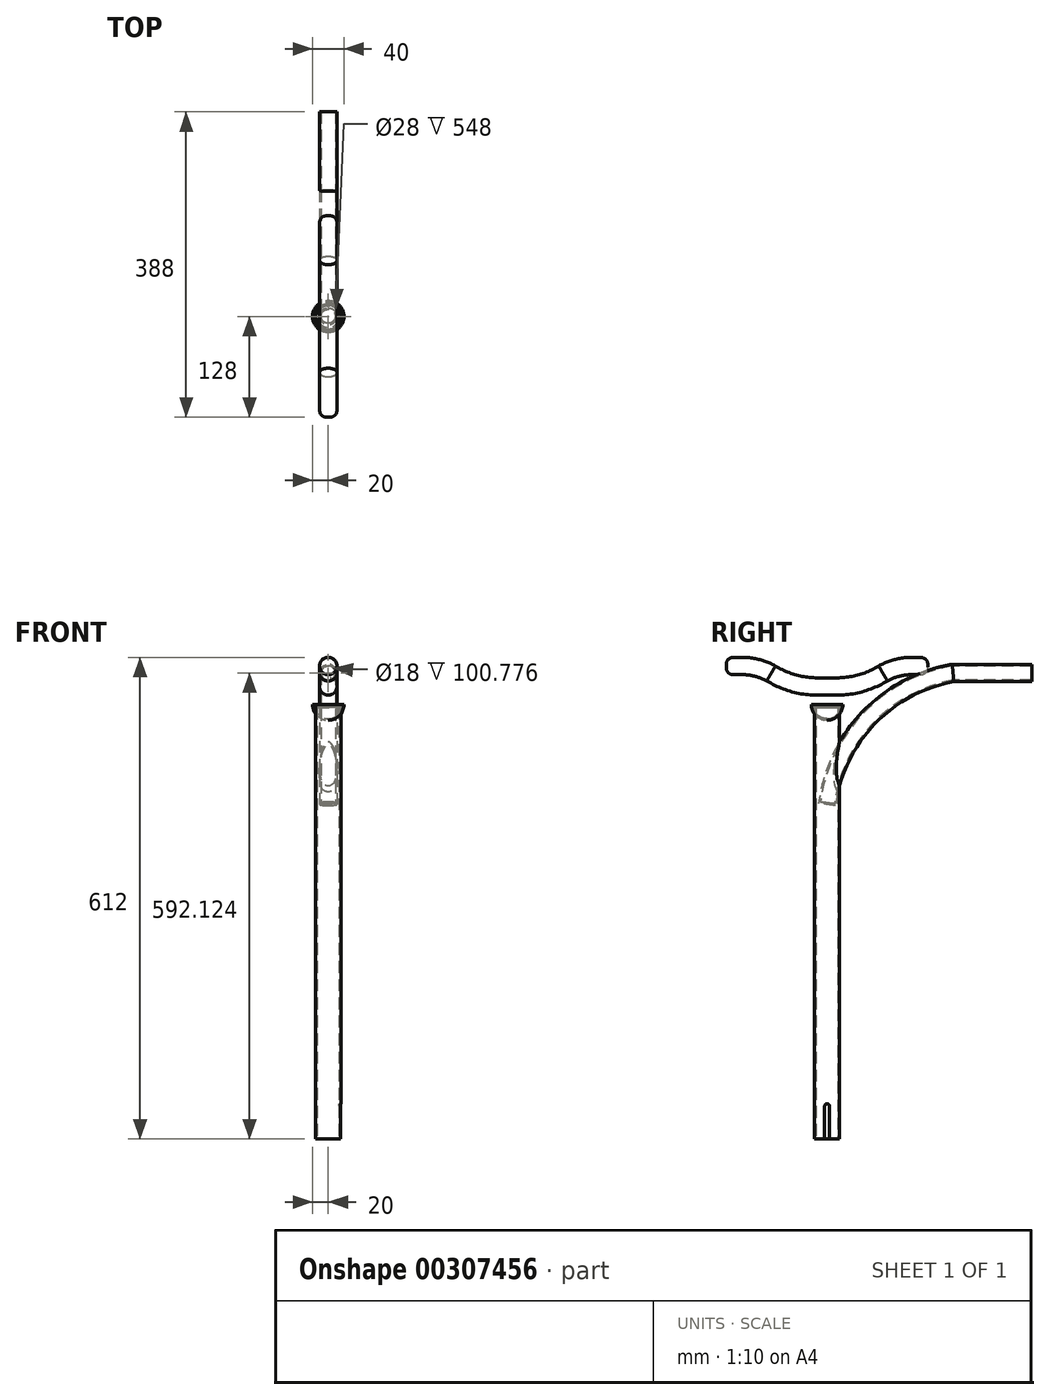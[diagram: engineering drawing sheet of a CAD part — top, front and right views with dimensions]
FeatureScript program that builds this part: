
annotation { "Feature Type Name" : "Feature", "Feature Type Description" : "" }
export const myFeature = defineFeature(function(context is Context, id is Id, definition is map)
    precondition{}
    {
        {
            var Q0;
            Q0=qCreatedBy(makeId("Top.planeOp"),FACE);
            var sketch = newSketch(context, id + "F0", { "sketchPlane" : qUnion([Q0])});
            skCircle(sketch, "E0", {"center": v(0, 0) * mm, "radius": 16 * mm});
            skSolve(sketch);
        }
        {
            var Q0;
            Q0 = qSketchRegion(id + "F0", true);
            extrude(context, id + "F1", {"entities" : qUnion([Q0]), "depth" : 550 * mm, "offsetDistance" : 25 * mm});
        }
        {
            var Q0;
            Q0=makeQuery(id+"F1.opExtrude","CAP_FACE",FACE,{"disambiguationData":[OSD([sQuery(id+"F0.wireOp",EDGE,"E0")])],"isStart":true});
            shell(context, id + "F2", {"entities" : qUnion([Q0]), "thickness" : 2 * mm});
        }
        {
            var Q0;
            Q0=qCreatedBy(makeId("Right.planeOp"),FACE);
            var sketch = newSketch(context, id + "F3", { "sketchPlane" : qUnion([Q0])});
            skLineSegment(sketch, "E1.bottom", {"start": v(0, 45) * mm, "end": v(0, 45) * mm});
            skLineSegment(sketch, "E1.top", {"start": v(-3, 0) * mm, "end": v(3, 0) * mm});
            skLineSegment(sketch, "E1.left", {"start": v(-3, 42) * mm, "end": v(-3, 0) * mm});
            skLineSegment(sketch, "E1.right", {"start": v(3, 42) * mm, "end": v(3, 0) * mm});
            skPoint(sketch, "E2.visualSharp", {"position": v(3, 45) * mm});
            skArc(sketch, "E2.filletArc", {"start": v(3, 42) * mm, "mid": v(2.12, 44.12) * mm, "end": v(0, 45) * mm});
            skPoint(sketch, "E3.visualSharp", {"position": v(-3, 45) * mm});
            skArc(sketch, "E3.filletArc", {"start": v(0, 45) * mm, "mid": v(-2.12, 44.12) * mm, "end": v(-3, 42) * mm});
            skSolve(sketch);
        }
        {
            var Q0;
            Q0 = qSketchRegion(id + "F3", true);
            extrude(context, id + "F4", {"entities" : qUnion([Q0]), "operationType" : NewBodyOperationType.REMOVE, "endBound" : BoundingType.THROUGH_ALL, "depth" : 25 * mm, "offsetDistance" : 25 * mm});
        }
        {
            var Q0;
            Q0=qCreatedBy(makeId("Right.planeOp"),FACE);
            var sketch = newSketch(context, id + "F5", { "sketchPlane" : qUnion([Q0])});
            skArc(sketch, "E4", {"start": v(160, 592.12) * mm, "mid": v(52.58, 534.92) * mm, "end": v(0, 425.16) * mm});
            skLineSegment(sketch, "E5", {"start": v(160, 592.12) * mm, "end": v(260, 592.12) * mm});
            skSolve(sketch);
        }
        {
            var Q0;
            Q0=qCreatedBy(makeId("Front.planeOp"),FACE);
            var Q1;
            Q1=sQuery(id+"F5.wireOp",VERTEX,"E5.end");
            cPlane(context, id + "F6", {"entities" : qUnion([Q0, Q1]), "cplaneType" : CPlaneType.PLANE_POINT, "offset" : 25 * mm, "width" : 150 * mm, "height" : 150 * mm});
        }
        {
            var Q0;
            Q0=qCreatedBy(id+"F6.planeOp",FACE);
            var sketch = newSketch(context, id + "F7", { "sketchPlane" : qUnion([Q0])});
            skCircle(sketch, "E6", {"center": v(0, 592.12) * mm, "radius": 11 * mm});
            skSolve(sketch);
        }
        {
            var Q0;
            Q0 = qSketchRegion(id + "F7", true);
            var Q1;
            Q1 = qConstructionFilter(qBodyType(qCreatedBy(id + "F5" ,EDGE), BodyType.WIRE), ConstructionObject.NO);
            sweep(context, id + "F8", {"operationType" : NewBodyOperationType.ADD, "profiles" : qUnion([Q0]), "path" : qUnion([Q1])});
        }
        {
            var Q0;
            Q0=makeQuery(id+"F8.opSweep","CAP_FACE",FACE,{"disambiguationData":[OSD([sQuery(id+"F5.wireOp",VERTEX,"E5.end"),sQuery(id+"F7.wireOp",EDGE,"E6")])],"isStart":true});
            shell(context, id + "F9", {"entities" : qUnion([Q0]), "thickness" : 2 * mm});
        }
        {
            var Q0;
            Q0=qCreatedBy(makeId("Right.planeOp"),FACE);
            var sketch = newSketch(context, id + "F10", { "sketchPlane" : qUnion([Q0])});
            skLineSegment(sketch, "E7", {"start": v(-128, 601) * mm, "end": v(-108, 601) * mm});
            skArc(sketch, "E8", {"start": v(-71.14, 591.58) * mm, "mid": v(-88.98, 598.6) * mm, "end": v(-108, 601) * mm});
            skLineSegment(sketch, "E9", {"start": v(-12.5, 575) * mm, "end": v(0, 575) * mm});
            skLineSegment(sketch, "E10", {"start": v(0, 0) * mm, "end": v(0, 575) * mm, "construction": true});
            skArc(sketch, "E11", {"start": v(-71.14, 591.58) * mm, "mid": v(-42.97, 579.22) * mm, "end": v(-12.5, 575) * mm});
            skLineSegment(sketch, "E12.MirrorCS", {"start": v(128, 601) * mm, "end": v(108, 601) * mm});
            skArc(sketch, "E13.MirrorCS", {"start": v(71.14, 591.58) * mm, "mid": v(88.98, 598.6) * mm, "end": v(108, 601) * mm});
            skArc(sketch, "E14.MirrorCS", {"start": v(71.14, 591.58) * mm, "mid": v(42.97, 579.22) * mm, "end": v(12.5, 575) * mm});
            skLineSegment(sketch, "E15.MirrorCS", {"start": v(12.5, 575) * mm, "end": v(0, 575) * mm});
            skSolve(sketch);
        }
        {
            var Q0;
            Q0=sQuery(id+"F10.wireOp",VERTEX,"E12.MirrorCS.start");
            var Q1;
            Q1=qCreatedBy(id+"F6.planeOp",FACE);
            cPlane(context, id + "F11", {"entities" : qUnion([Q0, Q1]), "cplaneType" : CPlaneType.PLANE_POINT, "offset" : 25 * mm, "width" : 150 * mm, "height" : 150 * mm});
        }
        {
            var Q0;
            Q0=qCreatedBy(id+"F11.planeOp",FACE);
            var sketch = newSketch(context, id + "F12", { "sketchPlane" : qUnion([Q0])});
            skCircle(sketch, "E16", {"center": v(0, 601) * mm, "radius": 11 * mm});
            skSolve(sketch);
        }
        {
            var Q0;
            Q0 = qSketchRegion(id + "F12", true);
            var Q1;
            Q1 = qConstructionFilter(qBodyType(qCreatedBy(id + "F10" ,EDGE), BodyType.WIRE), ConstructionObject.NO);
            sweep(context, id + "F13", {"profiles" : qUnion([Q0]), "path" : qUnion([Q1])});
        }
        {
            var Q0;
            Q0=makeQuery(id+"F13.opSweep","CAP_EDGE",EDGE,{"disambiguationData":[OSD([sQuery(id+"F10.wireOp",VERTEX,"E7.start"),sQuery(id+"F12.wireOp",EDGE,"E16")])],"isStart":false});
            var Q1;
            Q1=makeQuery(id+"F13.opSweep","CAP_EDGE",EDGE,{"disambiguationData":[OSD([sQuery(id+"F10.wireOp",VERTEX,"E12.MirrorCS.start"),sQuery(id+"F12.wireOp",EDGE,"E16")])],"isStart":true});
            fillet(context, id + "F14", {"entities" : qUnion([Q0, Q1]), "radius" : 10 * mm, "tangentPropagation" : true, "rho" : 0.5, "crossSection" : FilletCrossSection.CONIC, "allowEdgeOverflow" : false});
        }
        {
            var Q0;
            Q0=qCreatedBy(makeId("Right.planeOp"),FACE);
            var sketch = newSketch(context, id + "F15", { "sketchPlane" : qUnion([Q0])});
            skArc(sketch, "E17", {"start": v(-20, 552) * mm, "mid": v(-14.14, 537.86) * mm, "end": v(0, 532) * mm});
            skLineSegment(sketch, "E18", {"start": v(0, 552) * mm, "end": v(0, 532) * mm});
            skLineSegment(sketch, "E19", {"start": v(-20, 552) * mm, "end": v(0, 552) * mm});
            skPoint(sketch, "E20.orphan", {"position": v(0, 572) * mm});
            skSolve(sketch);
        }
        {
            var Q0;
            Q0 = qSketchRegion(id + "F15", true);
            var Q1;
            Q1=sQuery(id+"F15.wireOp",EDGE,"E18");
            revolve(context, id + "F16", {"entities" : qUnion([Q0]), "axis" : qUnion([Q1]), "revolveType" : RevolveType.FULL});
        }
        {
            var Q0;
            Q0=makeQuery(id+"F16.opRevolve","SWEPT_FACE",FACE,{"disambiguationData":[OSD([sQuery(id+"F15.wireOp",EDGE,"E19")])]});
            shell(context, id + "F17", {"entities" : qUnion([Q0]), "thickness" : 2 * mm});
        }
    });
